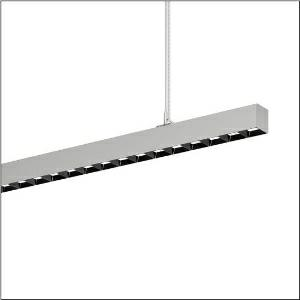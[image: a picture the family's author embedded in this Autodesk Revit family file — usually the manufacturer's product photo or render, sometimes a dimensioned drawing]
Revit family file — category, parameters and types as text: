
# Revit family: silica_21_51mx32tctds
name_source: partatom
category: Lighting Fixtures
units: mm (PartAtom-declared; Revit-internal decimal feet)

## family parameters
Cut with Voids When Loaded = No
Host = Face
Light Source = No
Part Type = Normal
Room Calculation Point = No
Round Connector Dimension = Use Diameter
Shared = No

## types (1)
- --- (1 x LED, 15540 lm, 133.6 W, 6500K)
    Apparent Load = 134 VA
    CIE Flux Codes = 84 99 100 60 100
    Color Rendering = 80
    Color Temperature = 6500K
    Default Elevation = 1800 mm
    Description = Silica 21, office luminaire, primary light control with darklight reflector, of PMMA, black, CAT 2 (L<= 3000cd/m²), light emission: direct/indirect distribution, primary light characteristic: symmetric, installation type: suspended mounting, LED, rated luminous flux: 15.540lm, luminous efficacy: 111lm/W, light colour: 8tw, colour temperature: 2700..6500K, control gear: DALI DT8, with terminal, 3+2-pole, max. 2.5mm², mains connection: 220..240V, AC, 50/60Hz, rated input power: 140.3W, luminaire housing, of aluminium, metallic grey (RAL 9006), length: 3.004mm, width: 53mm, height: 53mm, protection rating (complete): IP20, insulation class (complete): insulation class I (protective earthing), certification: CE, permissible operating ambient temperature: 0..+35°C, standard: EN 50419, packaging unit: 1 piece
    Height = 53 mm
    Lamp = 1 x LED
    Lamp Light Flux = 15540 lm
    Lamp Power = 133.6 W
    Lamp count = 1
    Length = 3004 mm
    Luminous efficacy = 116 lm/W
    Manufacturer = Siteco
    ModVariant = No
    Model = 51MX32TCTDS
    Mounting Place = Ceiling
    Mounting Type = Pendant
    Number of Poles = 1
    OnlyDefault = Yes
    Power Factor = 1
    Product Name = Silica 21
    Product group = office luminaire | ceiling pendant
    ProductGroupID = 903
    Protection Class = Protection class I
    Protection Degree = IP 20
    RLX_Detail_Level = 1
    RLX_Emergency_Light_Flux = 0 lm
    RLX_Emergency_Type = 0
    RLX_Emergency_Type_DB = No
    RlxData = <blob elided: 61873 chars, md5=ea7aa92a>
    Socket = socket
    Standby Power = 0 W
    System Light Flux = 15540 lm
    System Power = 134 W
    Type Comments = individual setting
    Type Image = l_1335859.jpg
    URL = http://relux.com
    VarID = @adj_139409
    Voltage = 0 V
    Weight = 0.00 kg
    Width = 53 mm

## geometry (parser evidence)
native form markers: Blend x4, Sweep x12
no freeform markers — native parametric forms only
